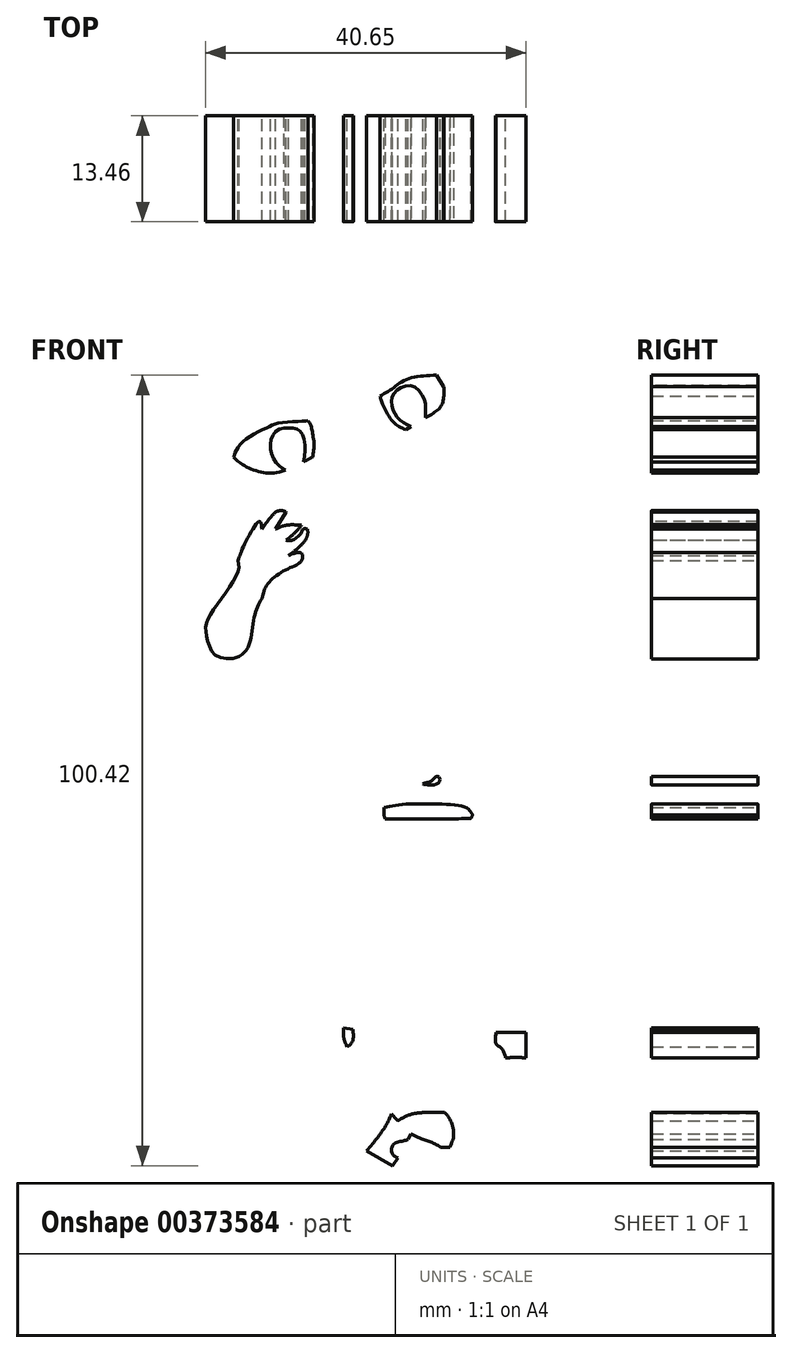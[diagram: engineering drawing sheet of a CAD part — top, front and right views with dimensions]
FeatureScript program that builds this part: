
annotation { "Feature Type Name" : "Feature", "Feature Type Description" : "" }
export const myFeature = defineFeature(function(context is Context, id is Id, definition is map)
    precondition{}
    {
        {
            var Q0;
            Q0=qCreatedBy(makeId("Front.planeOp"),FACE);
            var sketch = newSketch(context, id + "F0", { "sketchPlane" : qUnion([Q0])});
            skFitSpline(sketch, "E0", {"points": [v(-35.78, 54.46) * mm, v(-33.09, 59.85) * mm, v(-24.77, 66.06) * mm, v(-13.06, 67.81) * mm, v(-3.45, 65.7) * mm, v(-1.58, 65.82) * mm], "startDerivative": vector(10.86, 29.93) * mm, "endDerivative": vector(15.04, 3.36) * mm});
            skFitSpline(sketch, "E1", {"points": [v(-6.38, 64.18) * mm, v(-3.34, 64.3) * mm, v(-1.58, 65.82) * mm], "startDerivative": vector(6.22, -0.6) * mm, "endDerivative": vector(3.32, 3.98) * mm});
            skFitSpline(sketch, "E2", {"points": [v(-6.38, 64.18) * mm, v(-1.58, 62.66) * mm, v(2.4, 58.56) * mm, v(3.93, 55.63) * mm], "startDerivative": vector(14.2, -2.58) * mm, "endDerivative": vector(4.35, -9.84) * mm});
            skFitSpline(sketch, "E3", {"points": [v(3.93, 55.63) * mm, v(6.86, 54.23) * mm, v(8.96, 54.34) * mm], "startDerivative": vector(5.45, -3.31) * mm, "endDerivative": vector(4.6, 0.89) * mm});
            skFitSpline(sketch, "E4", {"points": [v(3.93, 54.21) * mm, v(5.68, 52.47) * mm, v(8.96, 54.34) * mm], "startDerivative": vector(3.48, -5.52) * mm, "endDerivative": vector(6.49, 5.4) * mm});
            skFitSpline(sketch, "E5", {"points": [v(5.68, 52.47) * mm, v(6.86, 48.72) * mm, v(6.86, 43.1) * mm, v(5.68, 41.7) * mm], "startDerivative": vector(3.82, -9.5) * mm, "endDerivative": vector(-5.74, -4.27) * mm});
            skFitSpline(sketch, "E6", {"points": [v(0, 51.42) * mm, v(1.35, 47.78) * mm, v(1.35, 45.1) * mm], "startDerivative": vector(3.15, -6.86) * mm, "endDerivative": vector(-0.56, -5.76) * mm});
            skFitSpline(sketch, "E7", {"points": [v(0, 51.42) * mm, v(3.93, 47.78) * mm, v(4.93, 43.33) * mm, v(5.68, 41.7) * mm], "startDerivative": vector(11.87, -7.83) * mm, "endDerivative": vector(3.7, -5.88) * mm});
            skFitSpline(sketch, "E8", {"points": [v(-7.7, 51.06) * mm, v(-5.13, 50.09) * mm, v(-0.67, 47.3) * mm, v(1.35, 45.1) * mm], "startDerivative": vector(8.03, -2.55) * mm, "endDerivative": vector(5.45, -7.1) * mm});
            skFitSpline(sketch, "E9", {"points": [v(-7.7, 51.06) * mm, v(-5.83, 48.77) * mm, v(-1.79, 45.96) * mm], "startDerivative": vector(3.67, -5.32) * mm, "endDerivative": vector(7.99, -4.9) * mm});
            skFitSpline(sketch, "E10", {"points": [v(-1.79, 45.96) * mm, v(-4.78, 45.96) * mm, v(-11.33, 49.25) * mm, v(-14.95, 51.76) * mm], "startDerivative": vector(-10.08, -1.7) * mm, "endDerivative": vector(-9.87, 7.2) * mm});
            skFitSpline(sketch, "E11", {"points": [v(-11.68, 45.1) * mm, v(-12.44, 48.14) * mm, v(-14.95, 51.76) * mm], "startDerivative": vector(-1, 6.65) * mm, "endDerivative": vector(-5.43, 6.69) * mm});
            skFitSpline(sketch, "E12", {"points": [v(-11.68, 45.1) * mm, v(-13.97, 47.7) * mm, v(-19.5, 51.76) * mm], "startDerivative": vector(-4.7, 6.12) * mm, "endDerivative": vector(-10.62, 7.16) * mm});
            skFitSpline(sketch, "E13", {"points": [v(-18.62, 45.1) * mm, v(-18.62, 48.14) * mm, v(-19.5, 51.76) * mm], "startDerivative": vector(0.4, 6.3) * mm, "endDerivative": vector(-2.13, 7.02) * mm});
            skFitSpline(sketch, "E14", {"points": [v(-20.14, 48.19) * mm, v(-19.3, 46.86) * mm, v(-18.62, 45.1) * mm], "startDerivative": vector(1.86, -2.65) * mm, "endDerivative": vector(1.2, -3.53) * mm});
            skFitSpline(sketch, "E15", {"points": [v(-22.6, 48.73) * mm, v(-20.78, 46.96) * mm, v(-19.55, 45.1) * mm], "startDerivative": vector(3.79, -3.33) * mm, "endDerivative": vector(2.3, -3.96) * mm});
            skFitSpline(sketch, "E16", {"points": [v(-20.14, 48.19) * mm, v(-19.3, 45.7) * mm, v(-19.55, 45.1) * mm], "startDerivative": vector(1.92, -4.36) * mm, "endDerivative": vector(-1.07, -1.52) * mm});
            skFitSpline(sketch, "E17", {"points": [v(-25.36, 50.22) * mm, v(-25.4, 46.4) * mm], "startDerivative": vector(-0.03, -3.81) * mm, "endDerivative": vector(-0.03, -3.81) * mm});
            skFitSpline(sketch, "E18", {"points": [v(-28.3, 48.16) * mm, v(-26.94, 47.5) * mm, v(-25.4, 46.4) * mm], "startDerivative": vector(2.87, -1.25) * mm, "endDerivative": vector(2.94, -2.24) * mm});
            skFitSpline(sketch, "E19", {"points": [v(-25.39, 47.04) * mm, v(-24.28, 48.16) * mm, v(-22.6, 48.73) * mm], "startDerivative": vector(2.06, 2.6) * mm, "endDerivative": vector(3.5, 0.8) * mm});
            skFitSpline(sketch, "E20", {"points": [v(-28.3, 48.16) * mm, v(-28.83, 43.89) * mm, v(-28.83, 43.03) * mm, v(-27.85, 38.2) * mm, v(-26.6, 36.06) * mm], "startDerivative": vector(-2.2, -17.32) * mm, "endDerivative": vector(5.7, -7.14) * mm});
            skFitSpline(sketch, "E21", {"points": [v(-28.3, 36.87) * mm, v(-27.46, 36.27) * mm, v(-26.6, 36.06) * mm], "startDerivative": vector(1.58, -1.34) * mm, "endDerivative": vector(1.82, -0.28) * mm});
            skFitSpline(sketch, "E22", {"points": [v(-30.88, 38.2) * mm, v(-29.25, 36.06) * mm, v(-27.37, 34.56) * mm], "startDerivative": vector(2.98, -4.44) * mm, "endDerivative": vector(4.04, -2.82) * mm});
            skFitSpline(sketch, "E23", {"points": [v(-28.3, 36.87) * mm, v(-27.85, 35.67) * mm, v(-27.37, 34.56) * mm], "startDerivative": vector(0.87, -2.39) * mm, "endDerivative": vector(0.98, -2.23) * mm});
            skFitSpline(sketch, "E24", {"points": [v(-30.88, 38.2) * mm, v(-30.28, 36.06) * mm, v(-28.3, 32.93) * mm], "startDerivative": vector(0.9, -4.76) * mm, "endDerivative": vector(4.12, -5.72) * mm});
            skFitSpline(sketch, "E25", {"points": [v(-30.88, 34.9) * mm, v(-29.77, 33.7) * mm, v(-28.3, 32.93) * mm], "startDerivative": vector(2.06, -2.62) * mm, "endDerivative": vector(3.1, -1.32) * mm});
            skFitSpline(sketch, "E26", {"points": [v(-30.88, 34.9) * mm, v(-30.26, 33.7) * mm, v(-29.1, 32.32) * mm], "startDerivative": vector(1.16, -2.58) * mm, "endDerivative": vector(2.37, -2.57) * mm});
            skFitSpline(sketch, "E27", {"points": [v(-31.59, 34.01) * mm, v(-30.54, 32.93) * mm, v(-29.1, 32.32) * mm], "startDerivative": vector(1.94, -2.42) * mm, "endDerivative": vector(3.02, -0.96) * mm});
            skFitSpline(sketch, "E28", {"points": [v(-31.59, 34.01) * mm, v(-30.88, 32.04) * mm, v(-29.47, 29.77) * mm, v(-27.85, 28.08) * mm], "startDerivative": vector(1.88, -6.17) * mm, "endDerivative": vector(5, -4.76) * mm});
            skFitSpline(sketch, "E29", {"points": [v(-32.7, 30.62) * mm, v(-31.27, 29.23) * mm, v(-29.1, 28.02) * mm, v(-27.85, 28.08) * mm], "startDerivative": vector(3.73, -4.02) * mm, "endDerivative": vector(4.29, 0.93) * mm});
            skFitSpline(sketch, "E30", {"points": [v(-32.7, 30.62) * mm, v(-33.17, 28.08) * mm, v(-32.15, 25.21) * mm, v(-29.1, 23.2) * mm, v(-27.37, 22.4) * mm], "startDerivative": vector(-2.96, -10.2) * mm, "endDerivative": vector(7.48, -3.45) * mm});
            skFitSpline(sketch, "E31", {"points": [v(-39.04, 37.32) * mm, v(-39.3, 32.93) * mm, v(-37.7, 28.98) * mm, v(-35.36, 26.2) * mm, v(-32.4, 23.59) * mm, v(-27.37, 22.4) * mm], "startDerivative": vector(-3.4, -21.75) * mm, "endDerivative": vector(24.84, -3.15) * mm});
            skFitSpline(sketch, "E32", {"points": [v(-39.04, 37.32) * mm, v(-39.93, 34.9) * mm, v(-41.09, 32.93) * mm], "startDerivative": vector(-1.58, -4.86) * mm, "endDerivative": vector(-2.54, -3.9) * mm});
            skFitSpline(sketch, "E33", {"points": [v(-35.78, 54.46) * mm, v(-39.04, 51.7) * mm, v(-41.02, 45.3) * mm, v(-41.02, 38.2) * mm, v(-41.09, 32.93) * mm], "startDerivative": vector(-16.55, -10.36) * mm, "endDerivative": vector(-0.72, -21.25) * mm});
            skFitSpline(sketch, "E34", {"points": [v(5.68, 41.7) * mm, v(6.42, 38.2) * mm, v(8.99, 34.9) * mm], "startDerivative": vector(0.72, -7.5) * mm, "endDerivative": vector(5.83, -6.1) * mm});
            skFitSpline(sketch, "E35", {"points": [v(8.99, 34.9) * mm, v(8.13, 34.01) * mm], "startDerivative": vector(-0.86, -0.89) * mm, "endDerivative": vector(-0.86, -0.89) * mm});
            skFitSpline(sketch, "E36", {"points": [v(-27.37, 22.4) * mm, v(-25.36, 20.57) * mm, v(-22.6, 19.8) * mm], "startDerivative": vector(3.73, -4.24) * mm, "endDerivative": vector(5.8, -0.97) * mm});
            skFitSpline(sketch, "E37", {"points": [v(-22.6, 19.8) * mm, v(-21.84, 21.8) * mm, v(-19.9, 24.77) * mm, v(-19.6, 23.8) * mm], "startDerivative": vector(1.48, 4.88) * mm, "endDerivative": vector(0.58, -6.35) * mm});
            skFitSpline(sketch, "E38", {"points": [v(-19.6, 23.8) * mm, v(-17.55, 26.1) * mm, v(-16.52, 25.98) * mm], "startDerivative": vector(3.39, 4.89) * mm, "endDerivative": vector(2.72, -1.06) * mm});
            skFitSpline(sketch, "E39", {"points": [v(-17.85, 23.8) * mm, v(-16.52, 25.98) * mm], "startDerivative": vector(1.33, 2.18) * mm, "endDerivative": vector(1.33, 2.18) * mm});
            skFitSpline(sketch, "E40", {"points": [v(-17.85, 23.8) * mm, v(-16.52, 24.3) * mm, v(-14.58, 24.3) * mm], "startDerivative": vector(2.72, 1.3) * mm, "endDerivative": vector(3.78, -0.29) * mm});
            skFitSpline(sketch, "E41", {"points": [v(-16.52, 22.4) * mm, v(-15.5, 23.24) * mm, v(-14.58, 24.3) * mm], "startDerivative": vector(2.13, 1.62) * mm, "endDerivative": vector(1.74, 2.17) * mm});
            skFitSpline(sketch, "E42", {"points": [v(-16.21, 20.46) * mm, v(-15.04, 21.35) * mm, v(-13.87, 22.8) * mm, v(-13.8, 23.8) * mm], "startDerivative": vector(3.34, 2.31) * mm, "endDerivative": vector(-0.34, 3.44) * mm});
            skFitSpline(sketch, "E43", {"points": [v(-16.52, 22.4) * mm, v(-15.73, 22.4) * mm, v(-14.58, 23.34) * mm, v(-14.38, 23.8) * mm, v(-13.8, 23.8) * mm], "startDerivative": vector(2.93, -0.64) * mm, "endDerivative": vector(3.34, -0.57) * mm});
            skFitSpline(sketch, "E44", {"points": [v(-19.6, 14.98) * mm, v(-18.89, 16.78) * mm, v(-16.52, 18.65) * mm, v(-14.58, 19.8) * mm, v(-14.58, 20.74) * mm, v(-16.21, 20.46) * mm], "startDerivative": vector(2.25, 9.04) * mm, "endDerivative": vector(-10.8, -4.04) * mm});
            skFitSpline(sketch, "E45", {"points": [v(-22.6, 19.8) * mm, v(-22.6, 18.51) * mm, v(-24.71, 14.98) * mm, v(-26.6, 12.03) * mm, v(-26.6, 10.16) * mm, v(-25.36, 7.7) * mm, v(-21.84, 8.1) * mm, v(-20.6, 12.48) * mm, v(-19.6, 14.98) * mm], "startDerivative": vector(2.63, -13.87) * mm, "endDerivative": vector(9.82, 18.02) * mm});
            skFitSpline(sketch, "E46", {"points": [v(-13.8, 37.83) * mm, v(-16.21, 38.2) * mm, v(-19.35, 38) * mm, v(-21.24, 37.1) * mm, v(-23.55, 35.39) * mm, v(-24.34, 34.01) * mm], "startDerivative": vector(-11.21, 2.22) * mm, "endDerivative": vector(-3.42, -8.47) * mm});
            skFitSpline(sketch, "E47", {"points": [v(-24.34, 34.01) * mm, v(-23.68, 33.33) * mm, v(-23.2, 32.93) * mm], "startDerivative": vector(1.23, -1.34) * mm, "endDerivative": vector(1.03, -0.8) * mm});
            skFitSpline(sketch, "E48", {"points": [v(-13.8, 37.83) * mm, v(-13.43, 37.6) * mm], "startDerivative": vector(0.37, -0.23) * mm, "endDerivative": vector(0.37, -0.23) * mm});
            skFitSpline(sketch, "E49", {"points": [v(-23.2, 32.93) * mm, v(-22.84, 33.82) * mm, v(-21.55, 35.3) * mm, v(-18.85, 36.72) * mm, v(-17.55, 37.26) * mm, v(-14.32, 37.51) * mm, v(-13.43, 37.6) * mm], "startDerivative": vector(2.32, 7) * mm, "endDerivative": vector(5.9, 0.82) * mm});
            skFitSpline(sketch, "E50", {"points": [v(-23.2, 32.93) * mm, v(-22.16, 32.07) * mm, v(-20.07, 31.13) * mm, v(-17.58, 31.02) * mm, v(-13.18, 32.93) * mm], "startDerivative": vector(5.1, -4.84) * mm, "endDerivative": vector(13.78, 7.2) * mm});
            skFitSpline(sketch, "E51", {"points": [v(-13.18, 32.93) * mm, v(-12.97, 34.38) * mm, v(-13.18, 36.06) * mm, v(-13.43, 37.05) * mm, v(-13.73, 37.56) * mm], "startDerivative": vector(1.07, 4.96) * mm, "endDerivative": vector(-1.82, 2.61) * mm});
            skFitSpline(sketch, "E52", {"points": [v(-16.59, 31.32) * mm, v(-17.53, 31.95) * mm, v(-18.37, 33.45) * mm, v(-18.45, 35.12) * mm, v(-17.58, 36.38) * mm, v(-16.01, 36.66) * mm, v(-14.94, 36.4) * mm, v(-14.2, 35.1) * mm, v(-14.22, 32.93) * mm, v(-14.33, 32.34) * mm], "startDerivative": vector(-9.83, 5) * mm, "endDerivative": vector(-1.64, -6.43) * mm});
            skFitSpline(sketch, "E53", {"points": [v(-17.58, 34.3) * mm, v(-17.55, 33.82) * mm, v(-17.21, 33.22) * mm, v(-16.8, 33.82) * mm, v(-16.46, 34.13) * mm, v(-16.42, 35.27) * mm, v(-16.8, 35.7) * mm, v(-17.55, 35.46) * mm, v(-17.79, 34.9) * mm, v(-17.75, 34.54) * mm, v(-17.58, 34.3) * mm]});
            skFitSpline(sketch, "E54", {"points": [v(-14.94, 34.22) * mm, v(-14.62, 34.17) * mm, v(-14.56, 33.22) * mm, v(-15, 33.22) * mm, v(-15.46, 33.22) * mm, v(-15.78, 33.22) * mm, v(-16, 33.45) * mm, v(-15.29, 33.53) * mm, v(-14.99, 33.82) * mm, v(-14.94, 34.22) * mm]});
            skFitSpline(sketch, "E55", {"points": [v(-21.86, 40.58) * mm, v(-20.54, 42) * mm, v(-19.37, 43) * mm, v(-17.81, 43.17) * mm, v(-17.4, 42.76) * mm, v(-17.79, 42.15) * mm, v(-19.19, 41.75) * mm, v(-20.51, 41.11) * mm, v(-21.86, 40.58) * mm]});
            skFitSpline(sketch, "E56", {"points": [v(-30.97, 28.2) * mm, v(-31.3, 28.04) * mm, v(-31.35, 27.36) * mm, v(-31.27, 26.59) * mm, v(-30.7, 25.8) * mm, v(-29.36, 25) * mm, v(-29.04, 24.94) * mm, v(-29.2, 25.39) * mm, v(-29.7, 25.86) * mm, v(-30.46, 26.52) * mm, v(-30.7, 26.9) * mm, v(-30.82, 27.76) * mm, v(-30.97, 28.2) * mm]});
            skFitSpline(sketch, "E57", {"points": [v(-28.79, 44.25) * mm, v(-27.31, 45.49) * mm, v(-25.77, 46.69) * mm], "startDerivative": vector(2.92, 2.5) * mm, "endDerivative": vector(3.1, 2.35) * mm});
            skFitSpline(sketch, "E58", {"points": [v(-23.28, 7.38) * mm, v(-23.34, 3.18) * mm, v(-22.86, 0) * mm, v(-22.26, -2.26) * mm, v(-22.26, -4.08) * mm, v(-21.65, -3.47) * mm, v(-20.8, -2.26) * mm], "startDerivative": vector(-0.82, -18.5) * mm, "endDerivative": vector(5.85, 8.57) * mm});
            skFitSpline(sketch, "E59", {"points": [v(-20.8, -2.26) * mm, v(-19.94, -4.93) * mm, v(-18.82, -7.88) * mm], "startDerivative": vector(1.69, -5.44) * mm, "endDerivative": vector(2.28, -5.8) * mm});
            skFitSpline(sketch, "E60", {"points": [v(-18.82, -7.88) * mm, v(-18.2, -6.6) * mm, v(-18, -5.44) * mm], "startDerivative": vector(1.37, 2.44) * mm, "endDerivative": vector(0.25, 2.45) * mm});
            skFitSpline(sketch, "E61", {"points": [v(-18, -5.44) * mm, v(-16.63, -7.12) * mm, v(-15.87, -7.32) * mm], "startDerivative": vector(2.26, -3.36) * mm, "endDerivative": vector(2, -0.14) * mm});
            skFitSpline(sketch, "E62", {"points": [v(-17.14, -1.42) * mm, v(-16.38, -3.5) * mm, v(-15.87, -7.32) * mm], "startDerivative": vector(1.96, -4.43) * mm, "endDerivative": vector(0.65, -7.25) * mm});
            skFitSpline(sketch, "E63", {"points": [v(-17.14, -1.42) * mm, v(-15.87, -2.06) * mm], "startDerivative": vector(1.27, -0.64) * mm, "endDerivative": vector(1.27, -0.64) * mm});
            skFitSpline(sketch, "E64", {"points": [v(-14.4, 8.3) * mm, v(-15.2, 6.36) * mm, v(-15.87, 3.77) * mm, v(-15.87, 0) * mm, v(-15.87, -2.06) * mm], "startDerivative": vector(-3.72, -8.42) * mm, "endDerivative": vector(-0.16, -8.38) * mm});
            skFitSpline(sketch, "E65", {"points": [v(-14.4, 8.3) * mm, v(-13.73, 6.87) * mm, v(-13.68, 3.62) * mm], "startDerivative": vector(1.93, -3.06) * mm, "endDerivative": vector(-0.36, -6.12) * mm});
            skFitSpline(sketch, "E66", {"points": [v(-9.36, 12.16) * mm, v(-9.97, 9.37) * mm, v(-11.09, 6.36) * mm, v(-13.68, 3.62) * mm], "startDerivative": vector(-1.82, -8.85) * mm, "endDerivative": vector(-8.2, -7.26) * mm});
            skFitSpline(sketch, "E67", {"points": [v(-9.36, 12.16) * mm, v(-8.44, 9.15) * mm, v(-6.35, 5.84) * mm, v(-5.23, 4.47) * mm], "startDerivative": vector(1.84, -8.43) * mm, "endDerivative": vector(3.88, -4.54) * mm});
            skFitSpline(sketch, "E68", {"points": [v(-5.23, 8.3) * mm, v(-5.23, 4.47) * mm], "startDerivative": vector(0, -3.83) * mm, "endDerivative": vector(0, -3.83) * mm});
            skFitSpline(sketch, "E69", {"points": [v(-5.23, 8.3) * mm, v(-2.64, 6.14) * mm, v(0, 4.47) * mm], "startDerivative": vector(5.02, -4.43) * mm, "endDerivative": vector(5.45, -3.23) * mm});
            skFitSpline(sketch, "E70", {"points": [v(-0.65, 6.2) * mm, v(0, 5.43) * mm, v(0, 4.47) * mm], "startDerivative": vector(1.62, -1.4) * mm, "endDerivative": vector(-0.32, -2.06) * mm});
            skFitSpline(sketch, "E71", {"points": [v(0, 5.43) * mm, v(0.87, 4.47) * mm, v(1.84, 2.89) * mm], "startDerivative": vector(1.94, -1.94) * mm, "endDerivative": vector(1.74, -3.11) * mm});
            skFitSpline(sketch, "E72", {"points": [v(0.77, 8.38) * mm, v(1.53, 6.6) * mm, v(1.94, 4.47) * mm, v(1.84, 2.89) * mm], "startDerivative": vector(2.45, -5.04) * mm, "endDerivative": vector(-0.63, -4.93) * mm});
            skFitSpline(sketch, "E73", {"points": [v(0.77, 8.38) * mm, v(3.16, 6.35) * mm, v(8.35, 3.5) * mm, v(10.23, 2.89) * mm], "startDerivative": vector(6.23, -6.11) * mm, "endDerivative": vector(6.35, -1.6) * mm});
            skFitSpline(sketch, "E74", {"points": [v(8.4, 5.43) * mm, v(9.47, 4.47) * mm, v(10.23, 2.89) * mm], "startDerivative": vector(2.43, -1.8) * mm, "endDerivative": vector(1.25, -3.26) * mm});
            skFitSpline(sketch, "E75", {"points": [v(9.47, 4.47) * mm, v(11.3, 3.17) * mm, v(14.43, 1.5) * mm, v(17.76, 0.9) * mm], "startDerivative": vector(5.9, -4.32) * mm, "endDerivative": vector(9.5, -0.91) * mm});
            skFitSpline(sketch, "E76", {"points": [v(17.76, 0.9) * mm, v(18.62, -1.15) * mm, v(18.96, -4.2) * mm, v(18.83, -4.8) * mm], "startDerivative": vector(2.57, -4.83) * mm, "endDerivative": vector(-0.84, -2.34) * mm});
            skFitSpline(sketch, "E77", {"points": [v(20.29, -1.88) * mm, v(20.25, -3.6) * mm, v(18.89, -4.64) * mm], "startDerivative": vector(0.57, -3.76) * mm, "endDerivative": vector(-3.37, -1.76) * mm});
            skFitSpline(sketch, "E78", {"points": [v(20.25, -3.6) * mm, v(19.66, -5.87) * mm, v(18.54, -8.86) * mm], "startDerivative": vector(-1.1, -4.78) * mm, "endDerivative": vector(-2.28, -5.73) * mm});
            skFitSpline(sketch, "E79", {"points": [v(18.54, -8.86) * mm, v(20.25, -7.54) * mm, v(21.54, -5.65) * mm], "startDerivative": vector(3.67, 2.44) * mm, "endDerivative": vector(2.32, 3.97) * mm});
            skFitSpline(sketch, "E80", {"points": [v(20.25, -8.86) * mm, v(21.11, -7.37) * mm, v(21.54, -5.65) * mm], "startDerivative": vector(1.96, 2.91) * mm, "endDerivative": vector(0.63, 3.5) * mm});
            skFitSpline(sketch, "E81", {"points": [v(20.25, -8.86) * mm, v(21.54, -7.7) * mm, v(22.57, -4.64) * mm], "startDerivative": vector(3.33, 2.19) * mm, "endDerivative": vector(1.4, 6.06) * mm});
            skFitSpline(sketch, "E82", {"points": [v(26.04, 4.47) * mm, v(25.9, 1.67) * mm, v(24.3, -2.57) * mm, v(22.57, -4.64) * mm], "startDerivative": vector(0.27, -8.4) * mm, "endDerivative": vector(-5.95, -5.77) * mm});
            skFitSpline(sketch, "E83", {"points": [v(20.25, 23.62) * mm, v(23.8, 18.8) * mm, v(26.54, 12.9) * mm, v(27.62, 7.28) * mm, v(26.04, 4.47) * mm], "startDerivative": vector(14.13, -17.43) * mm, "endDerivative": vector(-10.63, -12.77) * mm});
            skFitSpline(sketch, "E84", {"points": [v(10.72, 30.44) * mm, v(14.03, 28.92) * mm, v(20.25, 23.62) * mm], "startDerivative": vector(7.85, -2.76) * mm, "endDerivative": vector(10.99, -10.37) * mm});
            skFitSpline(sketch, "E85", {"points": [v(-18.43, -7.16) * mm, v(-17.63, -8.03) * mm, v(-16.42, -9) * mm], "startDerivative": vector(1.6, -1.88) * mm, "endDerivative": vector(2.41, -1.8) * mm});
            skFitSpline(sketch, "E86", {"points": [v(-16.42, -9) * mm, v(-16.15, -11.08) * mm, v(-15.76, -12.96) * mm, v(-14.27, -14.41) * mm], "startDerivative": vector(0.9, -6.15) * mm, "endDerivative": vector(5.24, -3.93) * mm});
            skFitSpline(sketch, "E87", {"points": [v(-14.27, -14.41) * mm, v(-8.74, -17.13) * mm, v(0.52, -18.6) * mm, v(10.03, -17.8) * mm, v(16.3, -15.35) * mm, v(18.33, -11.69) * mm, v(18.99, -9.75) * mm, v(20.25, -8.86) * mm], "startDerivative": vector(32.62, -19.16) * mm, "endDerivative": vector(18.52, 9.45) * mm});
            skFitSpline(sketch, "E88", {"points": [v(-4.09, -11.59) * mm, v(-3.93, -13.01) * mm, v(-1.75, -14.74) * mm, v(3.5, -14.95) * mm, v(6.4, -13.78) * mm, v(7.16, -12.5) * mm], "startDerivative": vector(-0.66, -9.66) * mm, "endDerivative": vector(3.65, 8.99) * mm});
            skFitSpline(sketch, "E89", {"points": [v(-4.09, -11.59) * mm, v(-1.75, -11.18) * mm, v(2.88, -11.13) * mm, v(6.34, -11.59) * mm, v(7.16, -12.5) * mm], "startDerivative": vector(9.19, 2.09) * mm, "endDerivative": vector(3.56, -6.23) * mm});
            skFitSpline(sketch, "E90", {"points": [v(-13.14, -2.74) * mm, v(-11.16, -1.46) * mm, v(-7.19, -1) * mm, v(-4.7, -1.87) * mm, v(-4.09, -3.2) * mm], "startDerivative": vector(7.11, 5.91) * mm, "endDerivative": vector(1.95, -7.59) * mm});
            skFitSpline(sketch, "E91", {"points": [v(-12.53, -3.9) * mm, v(-10.3, -2.69) * mm, v(-6.22, -2.58) * mm, v(-4.9, -3.6) * mm], "startDerivative": vector(5.8, 4.3) * mm, "endDerivative": vector(3.8, -4.53) * mm});
            skLineSegment(sketch, "E92", {"start": v(-13.14, -2.74) * mm, "end": v(-11.9, -2.74) * mm});
            skLineSegment(sketch, "E93", {"start": v(-11.9, -2.74) * mm, "end": v(-12.53, -3.9) * mm});
            skLineSegment(sketch, "E94", {"start": v(-4.9, -3.6) * mm, "end": v(-4.09, -3.2) * mm});
            skLineSegment(sketch, "E95", {"start": v(6.55, -2.23) * mm, "end": v(7.31, -3.2) * mm});
            skFitSpline(sketch, "E96", {"points": [v(6.55, -2.23) * mm, v(8.38, -1.16) * mm, v(9.6, -0.75) * mm, v(11.79, -0.65) * mm, v(15.15, -2.23) * mm], "startDerivative": vector(8, 5.03) * mm, "endDerivative": vector(10.7, -6.4) * mm});
            skFitSpline(sketch, "E97", {"points": [v(7.31, -3.2) * mm, v(8.74, -2.4) * mm, v(11.46, -2.07) * mm, v(14.47, -2.85) * mm, v(14.97, -3.2) * mm], "startDerivative": vector(5.6, 3.74) * mm, "endDerivative": vector(2.6, -2.24) * mm});
            skLineSegment(sketch, "E98", {"start": v(14.97, -3.2) * mm, "end": v(14.75, -2.5) * mm});
            skLineSegment(sketch, "E99", {"start": v(14.75, -2.5) * mm, "end": v(15.15, -2.23) * mm});
            skFitSpline(sketch, "E100", {"points": [v(-10.76, 3.1) * mm, v(-9.28, 4.27) * mm, v(-7.37, 4.73) * mm, v(-5.92, 4.45) * mm], "startDerivative": vector(3.94, 3.8) * mm, "endDerivative": vector(4.52, -1.34) * mm});
            skFitSpline(sketch, "E101", {"points": [v(-10.76, 3.1) * mm, v(-9.5, 3.3) * mm, v(-7.58, 3.56) * mm, v(-5.72, 3.53) * mm, v(-5.46, 4.12) * mm, v(-5.92, 4.45) * mm], "startDerivative": vector(5.75, 0.81) * mm, "endDerivative": vector(-4.31, 1.76) * mm});
            skFitSpline(sketch, "E102", {"points": [v(0.85, -8.55) * mm, v(1.9, -8.23) * mm, v(2.45, -7.68) * mm, v(2.9, -7.71) * mm, v(2.7, -8.55) * mm, v(0.85, -8.55) * mm]});
            skFitSpline(sketch, "E103", {"points": [v(-2.2, -18.44) * mm, v(-1.78, -19.48) * mm, v(0, -20.69) * mm, v(0.97, -21.23) * mm, v(1, -21.96) * mm, v(1.06, -23.14) * mm, v(1.3, -23.65) * mm], "startDerivative": vector(1.27, -6.3) * mm, "endDerivative": vector(2.3, -3.66) * mm});
            skFitSpline(sketch, "E104", {"points": [v(4.57, -18.5) * mm, v(4.57, -19.45) * mm, v(4.03, -20.42) * mm, v(2.27, -20.72) * mm, v(2.03, -21.63) * mm, v(2.03, -22.14) * mm, v(1.58, -22.93) * mm, v(1.3, -23.65) * mm], "startDerivative": vector(0.44, -6.45) * mm, "endDerivative": vector(-1.58, -5.57) * mm});
            skFitSpline(sketch, "E105", {"points": [v(2.05, -21.8) * mm, v(3.03, -22.55) * mm, v(4.74, -24.36) * mm], "startDerivative": vector(2.26, -1.57) * mm, "endDerivative": vector(3.07, -3.46) * mm});
            skFitSpline(sketch, "E106", {"points": [v(4.74, -24.36) * mm, v(5.52, -22.62) * mm, v(5.96, -21.76) * mm, v(6.3, -20.28) * mm, v(6.42, -19.7) * mm], "startDerivative": vector(2.6, 6.16) * mm, "endDerivative": vector(0.63, 2.75) * mm});
            skFitSpline(sketch, "E107", {"points": [v(4.74, -18.5) * mm, v(5.46, -18.87) * mm, v(6.42, -19.7) * mm], "startDerivative": vector(1.6, -0.7) * mm, "endDerivative": vector(1.74, -1.68) * mm});
            skFitSpline(sketch, "E108", {"points": [v(-1.58, -24.52) * mm, v(-0.83, -23.1) * mm, v(0, -22.03) * mm], "startDerivative": vector(1.38, 2.82) * mm, "endDerivative": vector(1.8, 2.13) * mm});
            skFitSpline(sketch, "E109", {"points": [v(0, -22.03) * mm, v(0.3, -22.55) * mm, v(0.87, -23.26) * mm, v(1.15, -23.38) * mm], "startDerivative": vector(0.72, -1.4) * mm, "endDerivative": vector(1.1, -0.25) * mm});
            skFitSpline(sketch, "E110", {"points": [v(1.43, -23.25) * mm, v(2.06, -23.12) * mm, v(2.38, -22.67) * mm, v(2.38, -22.47) * mm, v(2.6, -22.19) * mm], "startDerivative": vector(2.17, 0.05) * mm, "endDerivative": vector(1.29, 1.29) * mm});
            skFitSpline(sketch, "E111", {"points": [v(-4.86, 40.56) * mm, v(-3.95, 42.26) * mm, v(-0.8, 44.32) * mm, v(3.03, 44.62) * mm], "startDerivative": vector(2.4, 6.38) * mm, "endDerivative": vector(10.4, -0.42) * mm});
            skFitSpline(sketch, "E112", {"points": [v(-4.86, 40.56) * mm, v(-3.1, 41.6) * mm, v(-1.1, 42.86) * mm, v(2.6, 43.35) * mm], "startDerivative": vector(6.11, 3.24) * mm, "endDerivative": vector(10.26, 0.35) * mm});
            skFitSpline(sketch, "E113", {"points": [v(3.03, 44.62) * mm, v(3.5, 44.07) * mm, v(3.5, 41.9) * mm], "startDerivative": vector(1.5, -1.14) * mm, "endDerivative": vector(-0.4, -4.04) * mm});
            skFitSpline(sketch, "E114", {"points": [v(2.6, 43.35) * mm, v(3.5, 41.9) * mm], "startDerivative": vector(0.9, -1.45) * mm, "endDerivative": vector(0.9, -1.45) * mm});
            skFitSpline(sketch, "E115", {"points": [v(3.5, 41.9) * mm, v(3.5, 40.56) * mm, v(3.03, 39.25) * mm, v(1.35, 38.03) * mm, v(-1.32, 36.41) * mm], "startDerivative": vector(0.33, -6.36) * mm, "endDerivative": vector(-8.61, -5.3) * mm});
            skFitSpline(sketch, "E116", {"points": [v(-4.58, 40.71) * mm, v(-4.26, 39.7) * mm, v(-2.91, 37.42) * mm, v(-1.32, 36.41) * mm], "startDerivative": vector(0.9, -3.44) * mm, "endDerivative": vector(4.86, -2.15) * mm});
            skFitSpline(sketch, "E117", {"points": [v(1.21, 37.95) * mm, v(1.21, 38.84) * mm, v(1.06, 40.14) * mm, v(-0.32, 41.9) * mm, v(-2.2, 41.61) * mm, v(-3.11, 40.35) * mm, v(-2.88, 38.79) * mm, v(-2, 37.6) * mm, v(-0.65, 36.82) * mm], "startDerivative": vector(-0.04, 9.15) * mm, "endDerivative": vector(11.42, -5.53) * mm});
            skFitSpline(sketch, "E118", {"points": [v(-2.1, 40.9) * mm, v(-2.5, 40.56) * mm, v(-2.48, 39.94) * mm, v(-2.23, 39.74) * mm, v(-2.03, 39) * mm, v(-1.89, 38.6) * mm, v(-1.7, 38.86) * mm, v(-1.57, 39.3) * mm, v(-1.32, 39.31) * mm, v(-1.08, 39.92) * mm, v(-1.32, 40.88) * mm, v(-2.1, 40.9) * mm]});
            skFitSpline(sketch, "E119", {"points": [v(0.34, 39.56) * mm, v(0, 39.11) * mm, v(0.23, 38.86) * mm, v(0.38, 38.45) * mm, v(0.63, 38.54) * mm, v(0.74, 39.13) * mm, v(0.34, 39.56) * mm]});
            skFitSpline(sketch, "E120", {"points": [v(-2.2, -18.44) * mm, v(-3.13, -19.15) * mm, v(-3.83, -20.06) * mm, v(-3.9, -20.48) * mm], "startDerivative": vector(-2.44, -1.65) * mm, "endDerivative": vector(0.03, -1.67) * mm});
            skFitSpline(sketch, "E121", {"points": [v(-3.9, -20.48) * mm, v(-3.2, -21.57) * mm, v(-2.56, -22.72) * mm, v(-1.58, -24.52) * mm], "startDerivative": vector(2.36, -3.57) * mm, "endDerivative": vector(2.69, -4.92) * mm});
            skFitSpline(sketch, "E122", {"points": [v(-3.88, -20.21) * mm, v(-4.72, -20.6) * mm, v(-7.43, -22.8) * mm, v(-8, -23.82) * mm], "startDerivative": vector(-2.78, -0.96) * mm, "endDerivative": vector(-1.18, -3.3) * mm});
            skFitSpline(sketch, "E123", {"points": [v(-8, -23.82) * mm, v(-8, -27.3) * mm, v(-8, -29.13) * mm, v(-8.42, -31.26) * mm], "startDerivative": vector(-0.1, -9.5) * mm, "endDerivative": vector(-1.7, -7.06) * mm});
            skFitSpline(sketch, "E124", {"points": [v(-8.42, -31.26) * mm, v(-6.64, -32.13) * mm, v(-3.28, -31.87) * mm, v(-2.13, -31.77) * mm], "startDerivative": vector(4.64, -3.44) * mm, "endDerivative": vector(3.81, 0.18) * mm});
            skFitSpline(sketch, "E125", {"points": [v(3.74, -30.6) * mm, v(4.9, -31.26) * mm, v(8.78, -31.67) * mm, v(10.5, -31.26) * mm], "startDerivative": vector(3.44, -2.62) * mm, "endDerivative": vector(4.84, 1.76) * mm});
            skFitSpline(sketch, "E126", {"points": [v(6.42, -19.7) * mm, v(7.8, -20.79) * mm, v(9.74, -22.54) * mm, v(10.32, -23.97) * mm], "startDerivative": vector(3.98, -3.17) * mm, "endDerivative": vector(1.17, -4.82) * mm});
            skFitSpline(sketch, "E127", {"points": [v(10.32, -23.97) * mm, v(10.32, -26.7) * mm, v(10.32, -29.67) * mm, v(10.5, -31.26) * mm], "startDerivative": vector(0.05, -7.4) * mm, "endDerivative": vector(0.84, -5.33) * mm});
            skFitSpline(sketch, "E128", {"points": [v(13.83, -16.79) * mm, v(14.7, -21.7) * mm, v(15.07, -25.82) * mm, v(12.53, -26.67) * mm, v(10.32, -26.7) * mm], "startDerivative": vector(2.3, -15.84) * mm, "endDerivative": vector(-10.1, 0.17) * mm});
            skFitSpline(sketch, "E129", {"points": [v(-10.6, -16.4) * mm, v(-11.07, -21.47) * mm, v(-11.2, -26.7) * mm, v(-8, -27.3) * mm], "startDerivative": vector(-0.77, -13.29) * mm, "endDerivative": vector(13.92, 0.84) * mm});
            skFitSpline(sketch, "E130", {"points": [v(-2.13, -31.77) * mm, v(-2.13, -36.55) * mm, v(-0.86, -44.6) * mm, v(0, -48.5) * mm, v(0.96, -50.07) * mm], "startDerivative": vector(-0.95, -16.69) * mm, "endDerivative": vector(6.48, -8.72) * mm});
            skFitSpline(sketch, "E131", {"points": [v(-7.28, -31.96) * mm, v(-7.23, -34.16) * mm, v(-5.3, -41.85) * mm, v(-2.33, -50.5) * mm], "startDerivative": vector(-0.57, -9.22) * mm, "endDerivative": vector(7.34, -20.39) * mm});
            skFitSpline(sketch, "E132", {"points": [v(9.52, -31.56) * mm, v(8.57, -35.71) * mm, v(7.04, -42.63) * mm, v(4.9, -48.23) * mm], "startDerivative": vector(-3.26, -13.28) * mm, "endDerivative": vector(-6.75, -15.51) * mm});
            skFitSpline(sketch, "E133", {"points": [v(4.04, -30.83) * mm, v(4.04, -31.64) * mm, v(3.31, -37.55) * mm, v(2.3, -47.93) * mm], "startDerivative": vector(0.28, -4.57) * mm, "endDerivative": vector(-1.89, -21.56) * mm});
            skFitSpline(sketch, "E134", {"points": [v(13.72, -26.54) * mm, v(13.67, -29.99) * mm, v(13.73, -35.38) * mm, v(13.92, -40.15) * mm], "startDerivative": vector(-0.25, -11.06) * mm, "endDerivative": vector(0.61, -13.46) * mm});
            skFitSpline(sketch, "E135", {"points": [v(9.34, -32.31) * mm, v(9.82, -36.87) * mm, v(10.13, -40.15) * mm, v(10.13, -41.58) * mm, v(10.88, -42.2) * mm, v(11.37, -43.38) * mm], "startDerivative": vector(1.4, -15.85) * mm, "endDerivative": vector(2.14, -8.64) * mm});
            skFitSpline(sketch, "E136", {"points": [v(-7.32, -33.12) * mm, v(-7.71, -36.2) * mm, v(-7.71, -37.77) * mm, v(-7.8, -39.1) * mm, v(-8, -39.76) * mm, v(-8, -40.9) * mm, v(-8.49, -41.8) * mm, v(-9, -42.11) * mm, v(-9.21, -43.15) * mm], "startDerivative": vector(-2.64, -16.89) * mm, "endDerivative": vector(-0.53, -10.83) * mm});
            skFitSpline(sketch, "E137", {"points": [v(-9.21, -43.15) * mm, v(-7.79, -44.39) * mm, v(-5.55, -45.6) * mm, v(-3.81, -46.34) * mm], "startDerivative": vector(4.1, -4.02) * mm, "endDerivative": vector(5.4, -2.04) * mm});
            skFitSpline(sketch, "E138", {"points": [v(-0.5, -46.61) * mm, v(0.88, -46.72) * mm, v(2.4, -46.68) * mm], "startDerivative": vector(2.8, -0.29) * mm, "endDerivative": vector(3.04, 0.15) * mm});
            skFitSpline(sketch, "E139", {"points": [v(5.86, -46) * mm, v(8.42, -45.18) * mm, v(11.37, -43.38) * mm], "startDerivative": vector(5.45, 1.34) * mm, "endDerivative": vector(5.58, 3.83) * mm});
            skFitSpline(sketch, "E140", {"points": [v(13.92, -40.15) * mm, v(10.13, -40.15) * mm], "startDerivative": vector(-3.78, 0) * mm, "endDerivative": vector(-3.78, 0) * mm});
            skFitSpline(sketch, "E141", {"points": [v(13.92, -43.38) * mm, v(13.92, -40.15) * mm], "startDerivative": vector(0, 3.22) * mm, "endDerivative": vector(0, 3.22) * mm});
            skFitSpline(sketch, "E142", {"points": [v(11.37, -43.38) * mm, v(13.92, -43.38) * mm, v(18.25, -44.44) * mm, v(20.2, -46.46) * mm, v(20.62, -50.35) * mm, v(17, -52.54) * mm, v(10.75, -53.8) * mm, v(7.9, -54.12) * mm, v(4.9, -54.42) * mm], "startDerivative": vector(22.04, 1.3) * mm, "endDerivative": vector(-27.53, -2.77) * mm});
            skFitSpline(sketch, "E143", {"points": [v(4.9, -48.23) * mm, v(3.6, -50.27) * mm], "startDerivative": vector(-1.3, -2.05) * mm, "endDerivative": vector(-1.3, -2.05) * mm});
            skFitSpline(sketch, "E144", {"points": [v(2.3, -47.93) * mm, v(0.96, -50.07) * mm], "startDerivative": vector(-1.34, -2.14) * mm, "endDerivative": vector(-1.34, -2.14) * mm});
            skFitSpline(sketch, "E145", {"points": [v(3.6, -50.27) * mm, v(5.42, -48.46) * mm], "startDerivative": vector(1.82, 1.82) * mm, "endDerivative": vector(1.82, 1.82) * mm});
            skFitSpline(sketch, "E146", {"points": [v(5.42, -48.46) * mm, v(7.7, -48.06) * mm, v(10, -47.59) * mm, v(13.36, -45.61) * mm, v(17.63, -45.22) * mm, v(19.64, -46.8) * mm, v(20.03, -49.6) * mm, v(19.2, -50.87) * mm, v(18.09, -52.2) * mm], "startDerivative": vector(19.5, 3.85) * mm, "endDerivative": vector(-11.06, -13.53) * mm});
            skFitSpline(sketch, "E147", {"points": [v(-9.21, -43.15) * mm, v(-11.52, -42.73) * mm, v(-14.56, -42.73) * mm, v(-17.14, -43.15) * mm, v(-18.5, -44.68) * mm], "startDerivative": vector(-9.17, 2.14) * mm, "endDerivative": vector(-5.04, -8) * mm});
            skFitSpline(sketch, "E148", {"points": [v(-3.13, -50.5) * mm, v(-6.67, -48.46) * mm, v(-9.87, -46.86) * mm, v(-11.89, -45.97) * mm, v(-13.9, -44.42) * mm, v(-15.65, -43.9) * mm, v(-17.8, -44.42) * mm, v(-18.5, -44.68) * mm, v(-18.89, -45.97) * mm, v(-18.95, -47.93) * mm, v(-17.4, -50.27) * mm, v(-13.57, -52.11) * mm, v(-8.32, -54.33) * mm, v(-7.3, -54.89) * mm, v(-6.3, -55.22) * mm], "startDerivative": vector(-37.34, 22.1) * mm, "endDerivative": vector(22.17, -6.3) * mm});
            skFitSpline(sketch, "E149", {"points": [v(-3.13, -50.5) * mm, v(-4.12, -52.41) * mm, v(-6.3, -55.22) * mm], "startDerivative": vector(-1.91, -4.23) * mm, "endDerivative": vector(-4.33, -5.17) * mm});
            skFitSpline(sketch, "E150", {"points": [v(3.6, -50.27) * mm, v(4.4, -51.39) * mm, v(4.7, -53.63) * mm, v(4.3, -54.72) * mm, v(4.9, -54.42) * mm], "startDerivative": vector(3.34, -3.74) * mm, "endDerivative": vector(4.67, 2.99) * mm});
            skFitSpline(sketch, "E151", {"points": [v(-3.13, -50.5) * mm, v(-1.75, -51.98) * mm, v(-0.66, -53.04) * mm], "startDerivative": vector(2.65, -2.9) * mm, "endDerivative": vector(2.3, -2.17) * mm});
            skPoint(sketch, "E152.1.internal.snap0", {"position": v(-2.98, -64.76) * mm});
            skFitSpline(sketch, "E152", {"points": [v(-6.3, -55.22) * mm, v(-2.98, -57.07) * mm], "startDerivative": vector(3.32, -1.86) * mm, "endDerivative": vector(3.32, -1.86) * mm});
            skFitSpline(sketch, "E153", {"points": [v(-2.98, -57.07) * mm, v(-2.33, -56.05) * mm], "startDerivative": vector(0.65, 1.03) * mm, "endDerivative": vector(0.65, 1.03) * mm});
            skFitSpline(sketch, "E154", {"points": [v(-0.66, -53.04) * mm, v(-1.04, -53.75) * mm], "startDerivative": vector(-0.38, -0.7) * mm, "endDerivative": vector(-0.38, -0.7) * mm});
            skFitSpline(sketch, "E155", {"points": [v(-2.33, -56.05) * mm, v(-2.98, -55.66) * mm, v(-3.13, -54.89) * mm, v(-2.73, -54.25) * mm, v(-1.64, -53.92) * mm, v(-1.04, -53.75) * mm], "startDerivative": vector(-3.88, 1.48) * mm, "endDerivative": vector(3, 0.98) * mm});
            skFitSpline(sketch, "E156", {"points": [v(-2.33, -51.37) * mm, v(-0.44, -50.5) * mm, v(2.5, -50.27) * mm, v(3.6, -50.27) * mm], "startDerivative": vector(4.88, 2.98) * mm, "endDerivative": vector(3.74, 0) * mm});
            skFitSpline(sketch, "E157", {"points": [v(0.96, -50.07) * mm, v(0.96, -50.31) * mm], "startDerivative": vector(0, -0.24) * mm, "endDerivative": vector(0, -0.24) * mm});
            skFitSpline(sketch, "E158", {"points": [v(-0.66, -53.04) * mm, v(0.96, -53.75) * mm, v(3.6, -55.22) * mm, v(3.6, -58.14) * mm, v(1.76, -60.17) * mm, v(0, -60) * mm, v(-1.87, -58.44) * mm, v(-2.98, -57.07) * mm], "startDerivative": vector(11.36, -5.5) * mm, "endDerivative": vector(-8.07, 10.6) * mm});
            skFitSpline(sketch, "E159", {"points": [v(4.3, -54.72) * mm, v(3.1, -54.72) * mm], "startDerivative": vector(-1.2, 0) * mm, "endDerivative": vector(-1.2, 0) * mm});
            skFitSpline(sketch, "E160", {"points": [v(-9.87, -27.31) * mm, v(-9.64, -30.06) * mm, v(-9.32, -35.11) * mm, v(-9.2, -39.1) * mm, v(-9.2, -40.86) * mm, v(-8.78, -41.96) * mm], "startDerivative": vector(1.1, -12.59) * mm, "endDerivative": vector(3.94, -8.02) * mm});
            skFitSpline(sketch, "E161", {"points": [v(-9.21, -39.6) * mm, v(-8, -39.76) * mm], "startDerivative": vector(1.21, -0.17) * mm, "endDerivative": vector(1.21, -0.17) * mm});
            skFitSpline(sketch, "E162", {"points": [v(-6.76, 19.07) * mm, v(-7.3, 18.18) * mm, v(-9.2, 18.38) * mm, v(-9.32, 18.88) * mm, v(-9.87, 20.62) * mm, v(-8.78, 21.27) * mm, v(-8, 22.07) * mm, v(-7.3, 21.72) * mm, v(-7.3, 20.72) * mm, v(-6.76, 19.07) * mm]});
            skFitSpline(sketch, "E163", {"points": [v(-7.3, 21.72) * mm, v(-6.3, 22.22) * mm, v(-5.23, 21.72) * mm, v(-4.52, 20.67) * mm, v(-5.23, 19.52) * mm, v(-4.67, 18.88) * mm, v(-6.8, 18.65) * mm], "startDerivative": vector(6.38, 4.7) * mm, "endDerivative": vector(-15.2, -0.03) * mm});
            skFitSpline(sketch, "E164", {"points": [v(-4.9, 21.44) * mm, v(-3.87, 22.67) * mm, v(-2.33, 22.82) * mm, v(-1.04, 22.37) * mm, v(-1.04, 20.37) * mm, v(-1.75, 19.32) * mm, v(-2.98, 19.57) * mm, v(-3.97, 18.83) * mm, v(-4.67, 18.88) * mm], "startDerivative": vector(6.56, 10.96) * mm, "endDerivative": vector(-7.83, 2.8) * mm});
            skFitSpline(sketch, "E165", {"points": [v(-0.94, 20.8) * mm, v(0.96, 19.87) * mm, v(2.6, 20.37) * mm, v(3.6, 21.32) * mm, v(3.6, 22.87) * mm, v(4.3, 23.22) * mm, v(3.6, 24.62) * mm, v(2.6, 24.87) * mm, v(1.52, 24.91) * mm, v(1.52, 25.76) * mm, v(0.52, 25.66) * mm, v(-0.66, 24.07) * mm, v(-1.75, 22.75) * mm], "startDerivative": vector(18.42, -12.7) * mm, "endDerivative": vector(-12.24, -12.87) * mm});
            skFitSpline(sketch, "E166", {"points": [v(-9.32, 18.88) * mm, v(-9.95, 18.33) * mm, v(-11.52, 18.38) * mm, v(-11.52, 18.88) * mm, v(-12.45, 18.88) * mm, v(-12.3, 20.37) * mm, v(-12.45, 21.72) * mm, v(-11, 21.72) * mm, v(-9.95, 21.17) * mm, v(-9.32, 21.02) * mm], "startDerivative": vector(-4.1, -6.34) * mm, "endDerivative": vector(7.28, -1) * mm});
            skFitSpline(sketch, "E167", {"points": [v(-12.45, 19.54) * mm, v(-13.75, 18.88) * mm, v(-15, 19.39) * mm], "startDerivative": vector(-2.55, -1.92) * mm, "endDerivative": vector(-2.56, 1.63) * mm});
            skFitSpline(sketch, "E168", {"points": [v(-12.45, 21.72) * mm, v(-13.45, 22.37) * mm, v(-14.1, 22.37) * mm], "startDerivative": vector(-1.8, 1.46) * mm, "endDerivative": vector(-1.5, -0.24) * mm});
            skFitSpline(sketch, "E169", {"points": [v(3.6, 22.87) * mm, v(4.9, 22.37) * mm, v(5.95, 23.62) * mm, v(7.9, 24.12) * mm, v(6.86, 25.41) * mm, v(6.61, 26.41) * mm, v(5.42, 27.11) * mm, v(4.3, 26.91) * mm, v(2.6, 26.26) * mm, v(2.6, 24.87) * mm], "startDerivative": vector(13.83, -9.17) * mm, "endDerivative": vector(3.72, -14.8) * mm});
            skFitSpline(sketch, "E170", {"points": [v(7.33, 24.87) * mm, v(8.46, 25.26) * mm, v(7.9, 27.06) * mm, v(7.9, 28.06) * mm, v(7.06, 28.1) * mm, v(5.95, 28) * mm, v(5.42, 27.11) * mm], "startDerivative": vector(9.25, 0.85) * mm, "endDerivative": vector(-2.49, -7.07) * mm});
            skFitSpline(sketch, "E171", {"points": [v(8.15, 26.3) * mm, v(9.26, 26.16) * mm, v(10.5, 27.56) * mm, v(10.06, 28.56) * mm, v(10.1, 29.26) * mm, v(9.26, 29.76) * mm, v(8.46, 30.06) * mm, v(7.46, 29.7) * mm, v(6.76, 28.76) * mm, v(6.32, 28.1) * mm], "startDerivative": vector(8.92, -3.87) * mm, "endDerivative": vector(-4.58, -6.2) * mm});
            skFitSpline(sketch, "E172", {"points": [v(-13.8, 23.8) * mm, v(-12.93, 25.26) * mm, v(-14.03, 26.91) * mm, v(-14.56, 26.91) * mm, v(-14.73, 27.8) * mm, v(-16.27, 27.11) * mm, v(-16.85, 26.1) * mm], "startDerivative": vector(6.96, 6.62) * mm, "endDerivative": vector(-1.96, -6.05) * mm});
            skFitSpline(sketch, "E173", {"points": [v(-16.85, 25.43) * mm, v(-16.52, 25.25) * mm, v(-16.17, 24.33) * mm], "startDerivative": vector(0.93, -0.28) * mm, "endDerivative": vector(0.47, -1.8) * mm});
            skFitSpline(sketch, "E174", {"points": [v(-13.14, 25.98) * mm, v(-11.52, 26.55) * mm, v(-11.52, 28.47) * mm, v(-11.52, 29.5) * mm, v(-12.93, 29.38) * mm, v(-13.76, 29.63) * mm, v(-14.73, 27.8) * mm], "startDerivative": vector(11.52, 1.32) * mm, "endDerivative": vector(-4.72, -13.22) * mm});
            skFitSpline(sketch, "E175", {"points": [v(-11.42, 27.11) * mm, v(-9.87, 27.8) * mm, v(-9.87, 29.18) * mm, v(-10.89, 30.07) * mm, v(-11.05, 31.14) * mm, v(-13.27, 31.55) * mm, v(-13.76, 29.63) * mm], "startDerivative": vector(10.88, 2.35) * mm, "endDerivative": vector(0.53, -13.09) * mm});
            skLineSegment(sketch, "E176", {"start": v(4.04, -30.83) * mm, "end": v(4.04, -30.82) * mm});
            skLineSegment(sketch, "E177", {"start": v(-11.44, 31.44) * mm, "end": v(-10.43, 31.84) * mm});
            skLineSegment(sketch, "E178", {"start": v(-10.43, 31.84) * mm, "end": v(-9.62, 32.65) * mm});
            skLineSegment(sketch, "E179", {"start": v(-9.62, 32.65) * mm, "end": v(-8.93, 31.14) * mm});
            skLineSegment(sketch, "E180", {"start": v(-8.93, 31.14) * mm, "end": v(-7.6, 30.17) * mm});
            skLineSegment(sketch, "E181", {"start": v(-7.6, 30.17) * mm, "end": v(-8.2, 28.85) * mm});
            skLineSegment(sketch, "E182", {"start": v(-8.2, 28.85) * mm, "end": v(-9.66, 28.41) * mm});
            skPoint(sketch, "E183.5.internal.snap0", {"position": v(-9.27, 31.9) * mm});
            skFitSpline(sketch, "E183", {"points": [v(-9.27, 31.9) * mm, v(-8.97, 33.04) * mm, v(-7.65, 33.8) * mm, v(-7.3, 34.54) * mm, v(-6.15, 33.6) * mm, v(-6.06, 31.9) * mm, v(-6.88, 30.77) * mm, v(-7.6, 30.17) * mm], "startDerivative": vector(0.05, 9.48) * mm, "endDerivative": vector(-5.81, -4.4) * mm});
            skFitSpline(sketch, "E184", {"points": [v(-6.31, 31.42) * mm, v(-5.25, 30.73) * mm, v(-4.48, 31.24) * mm, v(-3.16, 31.24) * mm, v(-2.9, 33.04) * mm, v(-3.33, 34.5) * mm, v(-4.78, 34.2) * mm, v(-5.72, 35.05) * mm, v(-6.67, 34.24) * mm], "startDerivative": vector(9.51, -9.34) * mm, "endDerivative": vector(-8.3, -11.28) * mm});
            skFitSpline(sketch, "E185", {"points": [v(-3.02, 34.1) * mm, v(-2.34, 35.05) * mm, v(-0.42, 34.88) * mm, v(0.52, 34.5) * mm, v(0, 33.5) * mm, v(0.65, 32.44) * mm, v(-1.14, 31.76) * mm, v(-2.93, 31.57) * mm], "startDerivative": vector(3.8, 9.23) * mm, "endDerivative": vector(-9.74, -0.65) * mm});
            skFitSpline(sketch, "E186", {"points": [v(0, 32) * mm, v(0.6, 31.03) * mm, v(1.5, 31.33) * mm, v(1.6, 32.35) * mm, v(2.5, 33.55) * mm, v(1.68, 34.15) * mm, v(1.5, 35.1) * mm, v(0, 34.8) * mm], "startDerivative": vector(2.92, -8.97) * mm, "endDerivative": vector(-12.08, -4.77) * mm});
            skFitSpline(sketch, "E187", {"points": [v(7.88, 29.96) * mm, v(6.68, 30.17) * mm, v(6.51, 32.31) * mm, v(7.46, 32.1) * mm, v(8.13, 34.01) * mm, v(9.68, 32.78) * mm, v(11.18, 32.18) * mm, v(10.72, 30.44) * mm, v(10.1, 29.26) * mm], "startDerivative": vector(-12.44, -2.64) * mm, "endDerivative": vector(-4.85, -8.9) * mm});
            skFitSpline(sketch, "E188", {"points": [v(6.35, 31.16) * mm, v(4.5, 31.16) * mm, v(4.25, 32.1) * mm, v(3.13, 32.61) * mm, v(3.73, 34.01) * mm, v(3.99, 35.35) * mm, v(4.8, 34.88) * mm, v(5.74, 35.86) * mm, v(8.13, 34.01) * mm], "startDerivative": vector(-17.35, -3.37) * mm, "endDerivative": vector(15.34, -17.76) * mm});
            skFitSpline(sketch, "E189", {"points": [v(3.86, 32.31) * mm, v(3.4, 31.2) * mm, v(2.75, 31.63) * mm, v(1.5, 31.33) * mm], "startDerivative": vector(-1.13, -4.65) * mm, "endDerivative": vector(-3.69, -1.82) * mm});
            skFitSpline(sketch, "E190", {"points": [v(1.57, 34.7) * mm, v(2.53, 35.05) * mm, v(3, 34.4) * mm, v(3.99, 35.35) * mm], "startDerivative": vector(3.34, 2.23) * mm, "endDerivative": vector(2.97, 4.1) * mm});
            skFitSpline(sketch, "E191", {"points": [v(-3.93, -13.01) * mm, v(-0.7, -13.01) * mm, v(3.99, -13.01) * mm, v(6.98, -12.95) * mm], "startDerivative": vector(9.57, 0.01) * mm, "endDerivative": vector(9.1, 0.25) * mm});
            skFitSpline(sketch, "E192", {"points": [v(-4.09, -12.48) * mm, v(-2.92, -11.84) * mm, v(2.05, -11.59) * mm, v(6.68, -11.84) * mm], "startDerivative": vector(4.31, 3.46) * mm, "endDerivative": vector(11.2, -0.76) * mm});
            skFitSpline(sketch, "E193", {"points": [v(-2.33, -50.5) * mm, v(-1.97, -51.15) * mm], "startDerivative": vector(0.36, -0.65) * mm, "endDerivative": vector(0.36, -0.65) * mm});
            skLineSegment(sketch, "E194", {"start": v(-16.85, 26.1) * mm, "end": v(-16.85, 26.1) * mm});
            skLineSegment(sketch, "E195", {"start": v(18.89, -4.64) * mm, "end": v(18.88, -4.64) * mm});
            skSolve(sketch);
        }
        {
            var Q0;
            Q0=makeQuery(id+"F0.imprint","IMPRINT",FACE,{"disambiguationData":[TD([[makeQuery(id+"F0.imprint","IMPRINT",EDGE,{"derivedFrom":sQuery(id+"F0.wireOp",EDGE,"E102")}),-1.0]])]});
            var Q1;
            {var subQ0=sQuery(id+"F0.wireOp",EDGE,"E51");Q1=makeQuery(id+"F0.imprint","IMPRINT",FACE,{"disambiguationData":[TD([[makeQuery(id+"F0.imprint","IMPRINT",EDGE,{"derivedFrom":subQ0}),1.0]])]});}
            var Q2;
            {var subQ1=sQuery(id+"F0.wireOp",EDGE,"E114");Q2=makeQuery(id+"F0.imprint","IMPRINT",FACE,{"disambiguationData":[TD([[makeQuery(id+"F0.imprint","IMPRINT",EDGE,{"derivedFrom":subQ1}),-1.0]])]});}
            var Q3;
            {var subQ14=sQuery(id+"F0.wireOp",EDGE,"E37");Q3=makeQuery(id+"F0.imprint","IMPRINT",FACE,{"disambiguationData":[TD([[makeQuery(id+"F0.imprint","IMPRINT",EDGE,{"derivedFrom":subQ14}),-1.0]])]});}
            var Q4;
            {var subQ0=sQuery(id+"F0.wireOp",EDGE,"E191");var subQ1=sQuery(id+"F0.wireOp",EDGE,"E88");var subQ2=makeQuery(id+"F0.imprint","INTERSECT",VERTEX,{"disambiguationData":[OD(0.0)],"derivedFrom":[subQ1,subQ0]});Q4=makeQuery(id+"F0.imprint","IMPRINT",FACE,{"disambiguationData":[TD([[makeQuery(id+"F0.imprint","IMPRINT",EDGE,{"disambiguationData":[TD([[subQ2,-1.0]])],"derivedFrom":subQ1}),1.0]])]});}
            var Q5;
            {var subQ3=sQuery(id+"F0.wireOp",EDGE,"E192");Q5=makeQuery(id+"F0.imprint","IMPRINT",FACE,{"disambiguationData":[TD([[makeQuery(id+"F0.imprint","IMPRINT",EDGE,{"derivedFrom":subQ3}),-1.0]])]});}
            var Q6;
            {var subQ3=sQuery(id+"F0.wireOp",EDGE,"E192");Q6=makeQuery(id+"F0.imprint","IMPRINT",FACE,{"disambiguationData":[TD([[makeQuery(id+"F0.imprint","IMPRINT",EDGE,{"derivedFrom":subQ3}),1.0]])]});}
            var Q7;
            {var subQ7=sQuery(id+"F0.wireOp",EDGE,"E159");Q7=makeQuery(id+"F0.imprint","IMPRINT",FACE,{"disambiguationData":[TD([[makeQuery(id+"F0.imprint","IMPRINT",EDGE,{"derivedFrom":subQ7}),-1.0]])]});}
            var Q8;
            {var subQ3=sQuery(id+"F0.wireOp",EDGE,"E149");Q8=makeQuery(id+"F0.imprint","IMPRINT",FACE,{"disambiguationData":[TD([[makeQuery(id+"F0.imprint","IMPRINT",EDGE,{"derivedFrom":subQ3}),1.0]])]});}
            var Q9;
            {var subQ3=sQuery(id+"F0.wireOp",EDGE,"E140");Q9=makeQuery(id+"F0.imprint","IMPRINT",FACE,{"disambiguationData":[TD([[makeQuery(id+"F0.imprint","IMPRINT",EDGE,{"derivedFrom":subQ3}),1.0]])]});}
            var Q10;
            {var subQ3=sQuery(id+"F0.wireOp",EDGE,"E161");Q10=makeQuery(id+"F0.imprint","IMPRINT",FACE,{"disambiguationData":[TD([[makeQuery(id+"F0.imprint","IMPRINT",EDGE,{"derivedFrom":subQ3}),-1.0]])]});}
            extrude(context, id + "F1", {"entities" : qUnion([Q0, Q1, Q2, Q3, Q4, Q5, Q6, Q7, Q8, Q9, Q10]), "depth" : 13.46 * mm});
        }
    });
